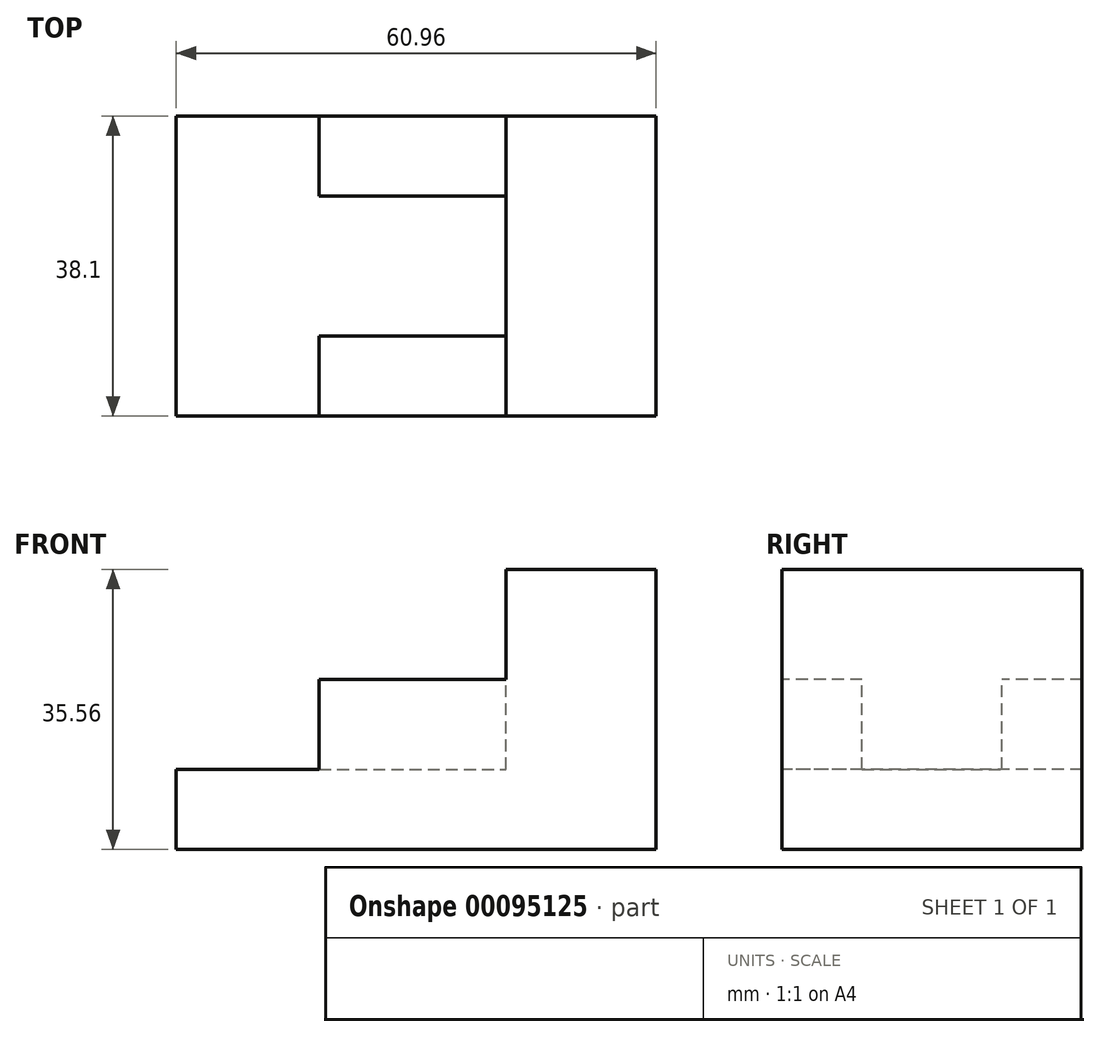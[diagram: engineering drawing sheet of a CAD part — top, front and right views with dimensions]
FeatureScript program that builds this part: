
annotation { "Feature Type Name" : "Feature", "Feature Type Description" : "" }
export const myFeature = defineFeature(function(context is Context, id is Id, definition is map)
    precondition{}
    {
        {
            var Q0;
            Q0=qCreatedBy(makeId("Top.planeOp"),FACE);
            var sketch = newSketch(context, id + "F0", { "sketchPlane" : qUnion([Q0])});
            skLineSegment(sketch, "E0.bottom", {"start": v(-30.48, 19.05) * mm, "end": v(30.48, 19.05) * mm});
            skLineSegment(sketch, "E0.top", {"start": v(-30.48, -19.05) * mm, "end": v(30.48, -19.05) * mm});
            skLineSegment(sketch, "E0.left", {"start": v(-30.48, 19.05) * mm, "end": v(-30.48, -19.05) * mm});
            skLineSegment(sketch, "E0.right", {"start": v(30.48, 19.05) * mm, "end": v(30.48, -19.05) * mm});
            skPoint(sketch, "E0.middle", {"position": v(0, 0) * mm});
            skSolve(sketch);
        }
        {
            var Q0;
            Q0 = qSketchRegion(id + "F0", true);
            extrude(context, id + "F1", {"entities" : qUnion([Q0]), "depth" : 10.16 * mm});
        }
        {
            var Q0;
            Q0=makeQuery(id+"F1.opExtrude","CAP_FACE",FACE,{"disambiguationData":[OSD([sQuery(id+"F0.wireOp",EDGE,"E0.bottom"),sQuery(id+"F0.wireOp",EDGE,"E0.top"),sQuery(id+"F0.wireOp",EDGE,"E0.left"),sQuery(id+"F0.wireOp",EDGE,"E0.right")])],"isStart":false});
            var sketch = newSketch(context, id + "F2", { "sketchPlane" : qUnion([Q0])});
            skLineSegment(sketch, "E1.bottom", {"start": v(11.43, 19.05) * mm, "end": v(30.48, 19.05) * mm});
            skLineSegment(sketch, "E1.top", {"start": v(11.43, -19.05) * mm, "end": v(30.48, -19.05) * mm});
            skLineSegment(sketch, "E1.left", {"start": v(11.43, 19.05) * mm, "end": v(11.43, -19.05) * mm});
            skLineSegment(sketch, "E1.right", {"start": v(30.48, 19.05) * mm, "end": v(30.48, -19.05) * mm});
            skSolve(sketch);
        }
        {
            var Q0;
            Q0 = qSketchRegion(id + "F2", true);
            extrude(context, id + "F3", {"entities" : qUnion([Q0]), "operationType" : NewBodyOperationType.ADD, "depth" : 25.4 * mm});
        }
        {
            var Q0;
            Q0=makeQuery(id+"F1.opExtrude","CAP_FACE",FACE,{"disambiguationData":[OSD([sQuery(id+"F0.wireOp",EDGE,"E0.bottom"),sQuery(id+"F0.wireOp",EDGE,"E0.top"),sQuery(id+"F0.wireOp",EDGE,"E0.left"),sQuery(id+"F0.wireOp",EDGE,"E0.right")])],"isStart":false});
            var sketch = newSketch(context, id + "F4", { "sketchPlane" : qUnion([Q0])});
            skLineSegment(sketch, "E2.bottom", {"start": v(11.43, 19.05) * mm, "end": v(-12.33, 19.05) * mm});
            skLineSegment(sketch, "E2.top", {"start": v(11.43, -19.05) * mm, "end": v(-12.33, -19.05) * mm});
            skLineSegment(sketch, "E2.left", {"start": v(11.43, 19.05) * mm, "end": v(11.43, -19.05) * mm});
            skLineSegment(sketch, "E2.right", {"start": v(-12.33, 19.05) * mm, "end": v(-12.33, -19.05) * mm});
            skSolve(sketch);
        }
        {
            var Q0;
            Q0 = qSketchRegion(id + "F4", true);
            extrude(context, id + "F5", {"entities" : qUnion([Q0]), "operationType" : NewBodyOperationType.ADD, "depth" : 11.43 * mm});
        }
        {
            var Q0;
            Q0=makeQuery(id+"F5.opExtrude","CAP_FACE",FACE,{"disambiguationData":[OSD([sQuery(id+"F4.wireOp",EDGE,"E2.bottom"),sQuery(id+"F4.wireOp",EDGE,"E2.top"),sQuery(id+"F4.wireOp",EDGE,"E2.left"),sQuery(id+"F4.wireOp",EDGE,"E2.right")])],"isStart":false});
            var sketch = newSketch(context, id + "F6", { "sketchPlane" : qUnion([Q0])});
            skLineSegment(sketch, "E3.bottom", {"start": v(11.43, 8.9) * mm, "end": v(-12.33, 8.89) * mm});
            skLineSegment(sketch, "E3.top", {"start": v(11.43, -8.89) * mm, "end": v(-12.33, -8.9) * mm});
            skLineSegment(sketch, "E3.left", {"start": v(11.43, 8.9) * mm, "end": v(11.43, -8.89) * mm});
            skLineSegment(sketch, "E3.right", {"start": v(-12.33, 8.89) * mm, "end": v(-12.33, -8.9) * mm});
            skSolve(sketch);
        }
        {
            var Q0;
            Q0 = qSketchRegion(id + "F6", true);
            var Q1;
            Q1=makeQuery(id+"F1.opExtrude","CAP_FACE",FACE,{"disambiguationData":[OSD([sQuery(id+"F0.wireOp",EDGE,"E0.bottom"),sQuery(id+"F0.wireOp",EDGE,"E0.top"),sQuery(id+"F0.wireOp",EDGE,"E0.left"),sQuery(id+"F0.wireOp",EDGE,"E0.right")])],"isStart":false});
            extrude(context, id + "F7", {"entities" : qUnion([Q0]), "operationType" : NewBodyOperationType.REMOVE, "endBound" : BoundingType.UP_TO_SURFACE, "oppositeDirection" : true, "endBoundEntityFace" : qUnion([Q1]), "depth" : 25.4 * mm});
        }
    });
